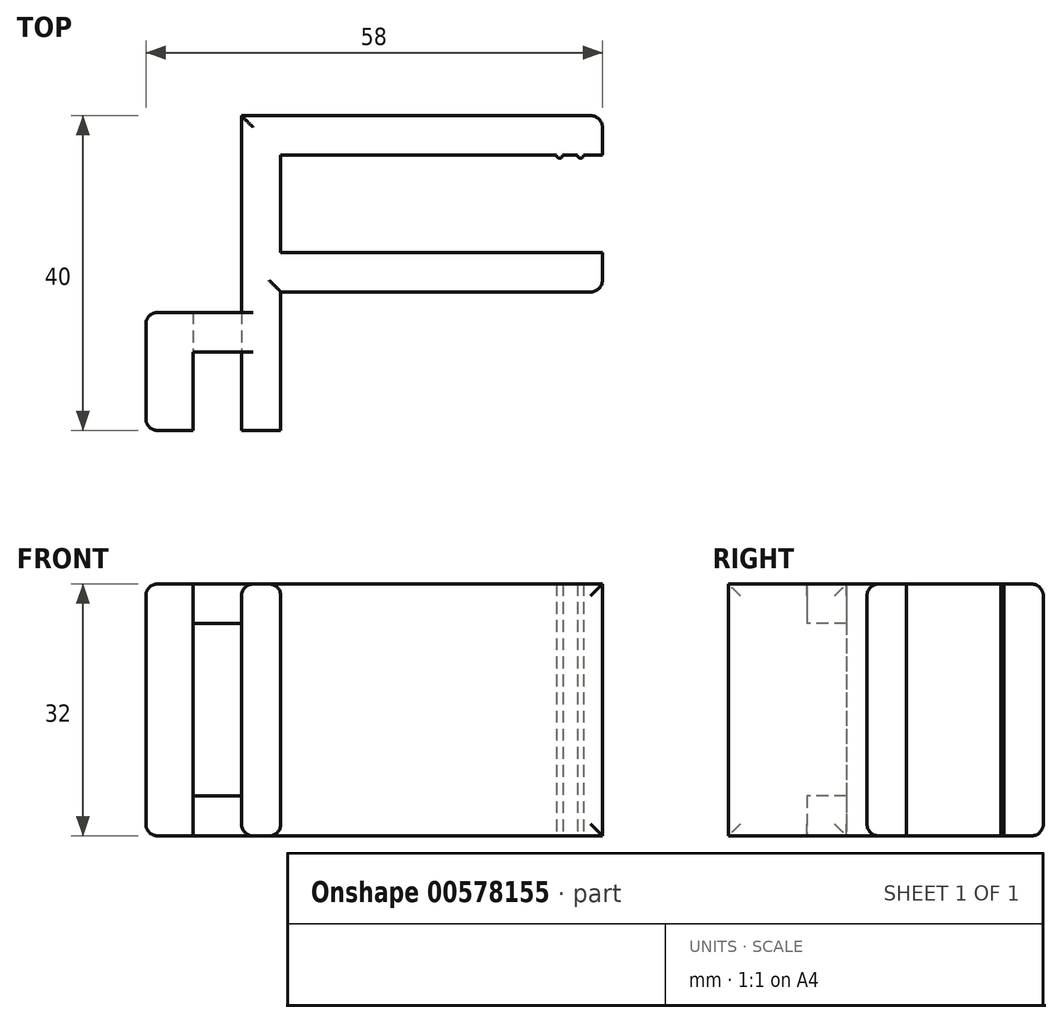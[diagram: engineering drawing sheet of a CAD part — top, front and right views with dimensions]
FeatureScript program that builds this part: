
annotation { "Feature Type Name" : "Feature", "Feature Type Description" : "" }
export const myFeature = defineFeature(function(context is Context, id is Id, definition is map)
    precondition{}
    {
        {
            var Q0;
            Q0=qCreatedBy(makeId("Top.planeOp"),FACE);
            var sketch = newSketch(context, id + "F0", { "sketchPlane" : qUnion([Q0])});
            skLineSegment(sketch, "E0.bottom", {"start": v(0, 0) * mm, "end": v(6, 0) * mm});
            skLineSegment(sketch, "E0.top", {"start": v(12.14, 40) * mm, "end": v(58, 40) * mm});
            skLineSegment(sketch, "E0.left", {"start": v(0, 0) * mm, "end": v(0, 15) * mm});
            skLineSegment(sketch, "E0.right", {"start": v(58, 25) * mm, "end": v(58, 30) * mm});
            skLineSegment(sketch, "E1", {"start": v(58, 35) * mm, "end": v(17.14, 35) * mm});
            skLineSegment(sketch, "E2", {"start": v(58, 25) * mm, "end": v(17.14, 25) * mm});
            skLineSegment(sketch, "E3", {"start": v(6, 0) * mm, "end": v(6, 15) * mm});
            skLineSegment(sketch, "E4", {"start": v(12.14, 0) * mm, "end": v(12.14, 25) * mm});
            skLineSegment(sketch, "E5", {"start": v(17.14, 0) * mm, "end": v(17.14, 25) * mm});
            skLineSegment(sketch, "E6", {"start": v(6, 10) * mm, "end": v(12.14, 10) * mm});
            skLineSegment(sketch, "E7", {"start": v(0, 15) * mm, "end": v(12.14, 15) * mm});
            skLineSegment(sketch, "E8", {"start": v(17.14, 30) * mm, "end": v(17.14, 35) * mm});
            skLineSegment(sketch, "E9", {"start": v(12.14, 25) * mm, "end": v(12.14, 40) * mm});
            skLineSegment(sketch, "E10.trimOffspring", {"start": v(12.14, 0) * mm, "end": v(17.14, 0) * mm});
            skLineSegment(sketch, "E11.trimOffspring", {"start": v(17.14, 30) * mm, "end": v(58, 30) * mm});
            skPoint(sketch, "E12.start.orphan", {"position": v(0, 30) * mm});
            skPoint(sketch, "E13.start.orphan", {"position": v(60.37, 35) * mm});
            skPoint(sketch, "E14.end.orphan", {"position": v(60.37, 40) * mm});
            skPoint(sketch, "E15.start.orphan", {"position": v(60.37, 30) * mm});
            skLineSegment(sketch, "E16.trimOffspring", {"start": v(58, 35) * mm, "end": v(58, 40) * mm});
            skArc(sketch, "E17", {"start": v(52.16, 35) * mm, "mid": v(52.56, 34.6) * mm, "end": v(52.96, 35) * mm});
            skArc(sketch, "E18", {"start": v(54.82, 35) * mm, "mid": v(55.22, 34.6) * mm, "end": v(55.62, 35) * mm});
            skSolve(sketch);
        }
        {
            var Q0;
            Q0=qSketchRegion(id+"F0",true);
            extrude(context, id + "F1", {"entities" : qUnion([Q0]), "depth" : 32 * mm, "offsetDistance" : 25 * mm});
        }
        {
            var Q0;
            Q0=makeQuery(id+"F1.opExtrude","SWEPT_FACE",FACE,{"disambiguationData":[OSD([sQuery(id+"F0.wireOp",EDGE,"E6")])]});
            var sketch = newSketch(context, id + "F2", { "sketchPlane" : qUnion([Q0])});
            skLineSegment(sketch, "E19.bottom", {"start": v(6, 0) * mm, "end": v(12.14, 0) * mm});
            skLineSegment(sketch, "E19.top", {"start": v(6, 5.07) * mm, "end": v(12.14, 5.07) * mm});
            skLineSegment(sketch, "E19.left", {"start": v(6, 0) * mm, "end": v(6, 5.07) * mm});
            skLineSegment(sketch, "E19.right", {"start": v(12.14, 0) * mm, "end": v(12.14, 5.07) * mm});
            skLineSegment(sketch, "E20.bottom", {"start": v(6, 32) * mm, "end": v(12.14, 32) * mm});
            skLineSegment(sketch, "E20.top", {"start": v(6, 27) * mm, "end": v(12.14, 27) * mm});
            skLineSegment(sketch, "E20.left", {"start": v(6, 32) * mm, "end": v(6, 27) * mm});
            skLineSegment(sketch, "E20.right", {"start": v(12.14, 32) * mm, "end": v(12.14, 27) * mm});
            skSolve(sketch);
        }
        {
            var Q0;
            {var subQ0=sQuery(id+"F2.wireOp",EDGE,"E19.top");Q0=makeQuery(id+"F2.imprint","IMPRINT",FACE,{"disambiguationData":[TD([[makeQuery(id+"F2.imprint","IMPRINT",EDGE,{"derivedFrom":subQ0}),1.0]])]});}
            extrude(context, id + "F3", {"entities" : qUnion([Q0]), "operationType" : NewBodyOperationType.REMOVE, "oppositeDirection" : true, "depth" : 5 * mm, "offsetDistance" : 25 * mm});
        }
        {
            var Q0;
            Q0=makeQuery(id+"F1.opExtrude","SWEPT_FACE",FACE,{"disambiguationData":[OSD([sQuery(id+"F0.wireOp",EDGE,"E2")])]});
            extrude(context, id + "F4", {"entities" : qUnion([Q0]), "operationType" : NewBodyOperationType.ADD, "depth" : 7.4 * mm, "offsetDistance" : 25 * mm});
        }
        {
            var Q0;
            Q0=makeQuery(id+"F1.opExtrude","SWEPT_FACE",FACE,{"disambiguationData":[OSD([sQuery(id+"F0.wireOp",EDGE,"E11.trimOffspring")])]});
            extrude(context, id + "F5", {"entities" : qUnion([Q0]), "operationType" : NewBodyOperationType.REMOVE, "oppositeDirection" : true, "depth" : 7.4 * mm, "offsetDistance" : 25 * mm});
        }
        {
            var Q0;
            Q0=makeQuery(id+"F1.opExtrude","CAP_EDGE",EDGE,{"disambiguationData":[OSD([sQuery(id+"F0.wireOp",EDGE,"E4"),sQuery(id+"F0.wireOp",EDGE,"E9")])],"isStart":false});
            var Q1;
            Q1=makeQuery(id+"F1.opExtrude","CAP_EDGE",EDGE,{"disambiguationData":[OSD([sQuery(id+"F0.wireOp",EDGE,"E4"),sQuery(id+"F0.wireOp",EDGE,"E9")])],"isStart":true});
            var Q2;
            Q2=makeQuery(id+"F1.opExtrude","CAP_EDGE",EDGE,{"disambiguationData":[OSD([sQuery(id+"F0.wireOp",EDGE,"E4")])],"isStart":true});
            var Q3;
            Q3=makeQuery(id+"F1.opExtrude","SWEPT_FACE",FACE,{"disambiguationData":[OSD([sQuery(id+"F0.wireOp",EDGE,"E0.left")])]});
            var Q4;
            Q4=makeQuery(id+"F1.opExtrude","CAP_EDGE",EDGE,{"disambiguationData":[OSD([sQuery(id+"F0.wireOp",EDGE,"E4")])],"isStart":false});
            var Q5;
            Q5=makeQuery(id+"F1.opExtrude","CAP_EDGE",EDGE,{"disambiguationData":[OSD([sQuery(id+"F0.wireOp",EDGE,"E5")])],"isStart":true});
            var Q6;
            {var subQ0=sQuery(id+"F0.wireOp",EDGE,"E11.trimOffspring");var subQ1=sQuery(id+"F0.wireOp",EDGE,"E8");Q6=makeQuery(id+"F5.boolean.opBoolean","MERGE",EDGE,{"derivedFrom":[makeQuery(id+"F1.opExtrude","CAP_EDGE",EDGE,{"disambiguationData":[OSD([subQ1])],"isStart":true}),makeQuery(id+"F5.opExtrude","SWEPT_EDGE",EDGE,{"disambiguationData":[OSD([subQ1,subQ0]),TDD([makeQuery(id+"F1.opExtrude","CAP_VERTEX",VERTEX,{"disambiguationData":[OSD([subQ1,subQ0])],"isStart":true})])]})]});}
            var Q7;
            {var subQ0=sQuery(id+"F0.wireOp",EDGE,"E11.trimOffspring");var subQ1=sQuery(id+"F0.wireOp",EDGE,"E8");Q7=makeQuery(id+"F5.boolean.opBoolean","MERGE",EDGE,{"derivedFrom":[makeQuery(id+"F1.opExtrude","CAP_EDGE",EDGE,{"disambiguationData":[OSD([subQ1])],"isStart":false}),makeQuery(id+"F5.opExtrude","SWEPT_EDGE",EDGE,{"disambiguationData":[OSD([subQ1,subQ0]),TDD([makeQuery(id+"F1.opExtrude","CAP_VERTEX",VERTEX,{"disambiguationData":[OSD([subQ1,subQ0])],"isStart":false})])]})]});}
            var Q8;
            Q8=makeQuery(id+"F1.opExtrude","CAP_EDGE",EDGE,{"disambiguationData":[OSD([sQuery(id+"F0.wireOp",EDGE,"E5")])],"isStart":false});
            var Q9;
            {var subQ0=sQuery(id+"F0.wireOp",EDGE,"E2");Q9=makeQuery(id+"F4.opExtrude","CAP_EDGE",EDGE,{"disambiguationData":[OSD([subQ0]),TDD([makeQuery(id+"F1.opExtrude","CAP_EDGE",EDGE,{"disambiguationData":[OSD([subQ0])],"isStart":false})])],"isStart":false});}
            var Q10;
            {var subQ0=sQuery(id+"F0.wireOp",EDGE,"E2");Q10=makeQuery(id+"F4.opExtrude","CAP_EDGE",EDGE,{"disambiguationData":[OSD([subQ0]),TDD([makeQuery(id+"F1.opExtrude","CAP_EDGE",EDGE,{"disambiguationData":[OSD([subQ0])],"isStart":true})])],"isStart":false});}
            var Q11;
            Q11=makeQuery(id+"F1.opExtrude","CAP_EDGE",EDGE,{"disambiguationData":[OSD([sQuery(id+"F0.wireOp",EDGE,"E0.top")])],"isStart":true});
            var Q12;
            Q12=makeQuery(id+"F1.opExtrude","CAP_EDGE",EDGE,{"disambiguationData":[OSD([sQuery(id+"F0.wireOp",EDGE,"E0.top")])],"isStart":false});
            var Q13;
            Q13=makeQuery(id+"F1.opExtrude","SWEPT_EDGE",EDGE,{"disambiguationData":[OSD([sQuery(id+"F0.wireOp",EDGE,"E0.top"),sQuery(id+"F0.wireOp",EDGE,"E16.trimOffspring")])]});
            var Q14;
            Q14=makeQuery(id+"F4.opExtrude","CAP_EDGE",EDGE,{"disambiguationData":[OSD([sQuery(id+"F0.wireOp",EDGE,"E0.right"),sQuery(id+"F0.wireOp",EDGE,"E2")])],"isStart":false});
            fillet(context, id + "F6", {"entities" : qUnion([Q0, Q1, Q2, Q3, Q4, Q5, Q6, Q7, Q8, Q9, Q10, Q11, Q12, Q13, Q14]), "radius" : 1.5 * mm, "tangentPropagation" : true, "allowEdgeOverflow" : false});
        }
    });
